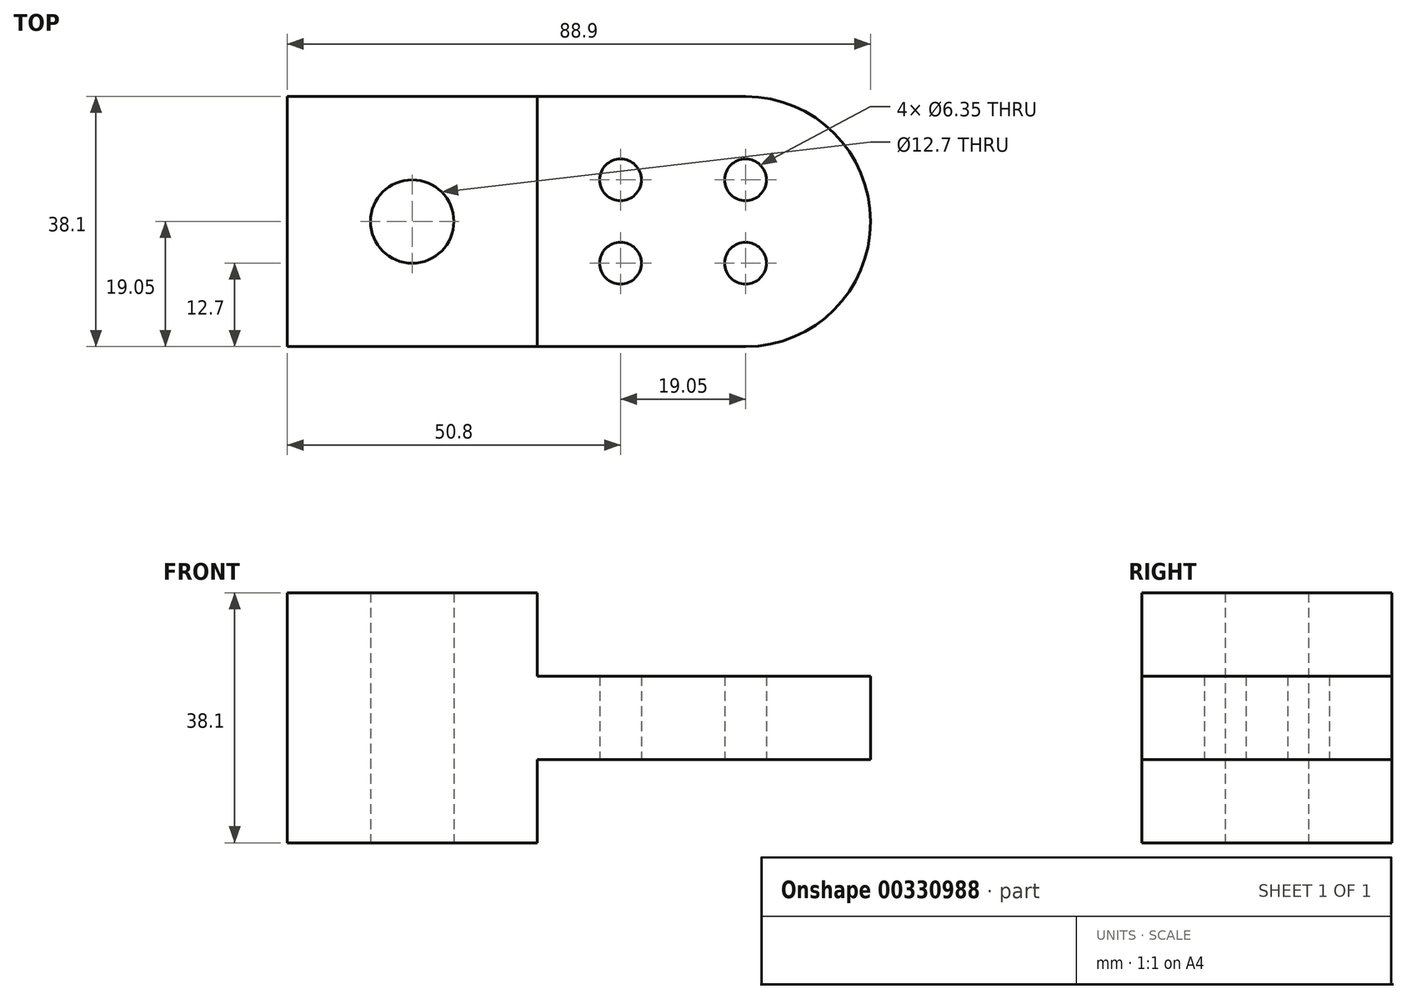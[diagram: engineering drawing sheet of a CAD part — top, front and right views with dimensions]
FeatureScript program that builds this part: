
annotation { "Feature Type Name" : "Feature", "Feature Type Description" : "" }
export const myFeature = defineFeature(function(context is Context, id is Id, definition is map)
    precondition{}
    {
        {
            var Q0;
            Q0=qCreatedBy(makeId("Front.planeOp"),FACE);
            var sketch = newSketch(context, id + "F0", { "sketchPlane" : qUnion([Q0])});
            skLineSegment(sketch, "E0", {"start": v(0, 0) * mm, "end": v(0, 38.1) * mm});
            skLineSegment(sketch, "E1", {"start": v(0, 38.1) * mm, "end": v(38.1, 38.1) * mm});
            skLineSegment(sketch, "E2", {"start": v(38.1, 38.1) * mm, "end": v(38.1, 25.4) * mm});
            skLineSegment(sketch, "E3", {"start": v(38.1, 25.4) * mm, "end": v(88.9, 25.4) * mm});
            skLineSegment(sketch, "E4", {"start": v(88.9, 25.4) * mm, "end": v(88.9, 12.7) * mm});
            skLineSegment(sketch, "E5", {"start": v(88.9, 12.7) * mm, "end": v(38.1, 12.7) * mm});
            skLineSegment(sketch, "E6", {"start": v(38.1, 12.7) * mm, "end": v(38.1, 0) * mm});
            skLineSegment(sketch, "E7", {"start": v(38.1, 0) * mm, "end": v(0, 0) * mm});
            skSolve(sketch);
        }
        {
            var Q0;
            Q0 = qSketchRegion(id + "F0", true);
            extrude(context, id + "F1", {"entities" : qUnion([Q0]), "endBound" : BoundingType.SYMMETRIC, "oppositeDirection" : true, "depth" : 38.1 * mm});
        }
        {
            var Q0;
            Q0=qCreatedBy(makeId("Top.planeOp"),FACE);
            var sketch = newSketch(context, id + "F2", { "sketchPlane" : qUnion([Q0])});
            skLineSegment(sketch, "E8", {"start": v(0, 0) * mm, "end": v(93.4, 0) * mm, "construction": true});
            skPoint(sketch, "E9", {"position": v(19.05, 0) * mm});
            skCircle(sketch, "E10", {"center": v(19.05, 0) * mm, "radius": 6.35 * mm});
            skPoint(sketch, "E11", {"position": v(50.8, 0) * mm});
            skPoint(sketch, "E12", {"position": v(69.85, 0) * mm});
            skPoint(sketch, "E13", {"position": v(50.8, 6.35) * mm});
            skPoint(sketch, "E14", {"position": v(50.8, -6.35) * mm});
            skPoint(sketch, "E15", {"position": v(69.85, -6.35) * mm});
            skPoint(sketch, "E16", {"position": v(69.85, 6.35) * mm});
            skCircle(sketch, "E17", {"center": v(50.8, 6.35) * mm, "radius": 3.18 * mm});
            skCircle(sketch, "E18", {"center": v(50.8, -6.35) * mm, "radius": 3.18 * mm});
            skCircle(sketch, "E19", {"center": v(69.85, 6.35) * mm, "radius": 3.18 * mm});
            skCircle(sketch, "E20", {"center": v(69.85, -6.35) * mm, "radius": 3.18 * mm});
            skArc(sketch, "E21", {"start": v(69.85, -19.05) * mm, "mid": v(88.9, 0) * mm, "end": v(69.85, 19.05) * mm});
            skLineSegment(sketch, "E22", {"start": v(69.85, 19.05) * mm, "end": v(88.9, 19.05) * mm});
            skLineSegment(sketch, "E23", {"start": v(88.9, 19.05) * mm, "end": v(88.9, -19.05) * mm});
            skLineSegment(sketch, "E24", {"start": v(69.85, -19.05) * mm, "end": v(88.9, -19.05) * mm});
            skSolve(sketch);
        }
        {
            var Q0;
            Q0 = qSketchRegion(id + "F2", true);
            extrude(context, id + "F3", {"entities" : qUnion([Q0]), "operationType" : NewBodyOperationType.REMOVE, "endBound" : BoundingType.THROUGH_ALL, "depth" : 25.4 * mm});
        }
    });
